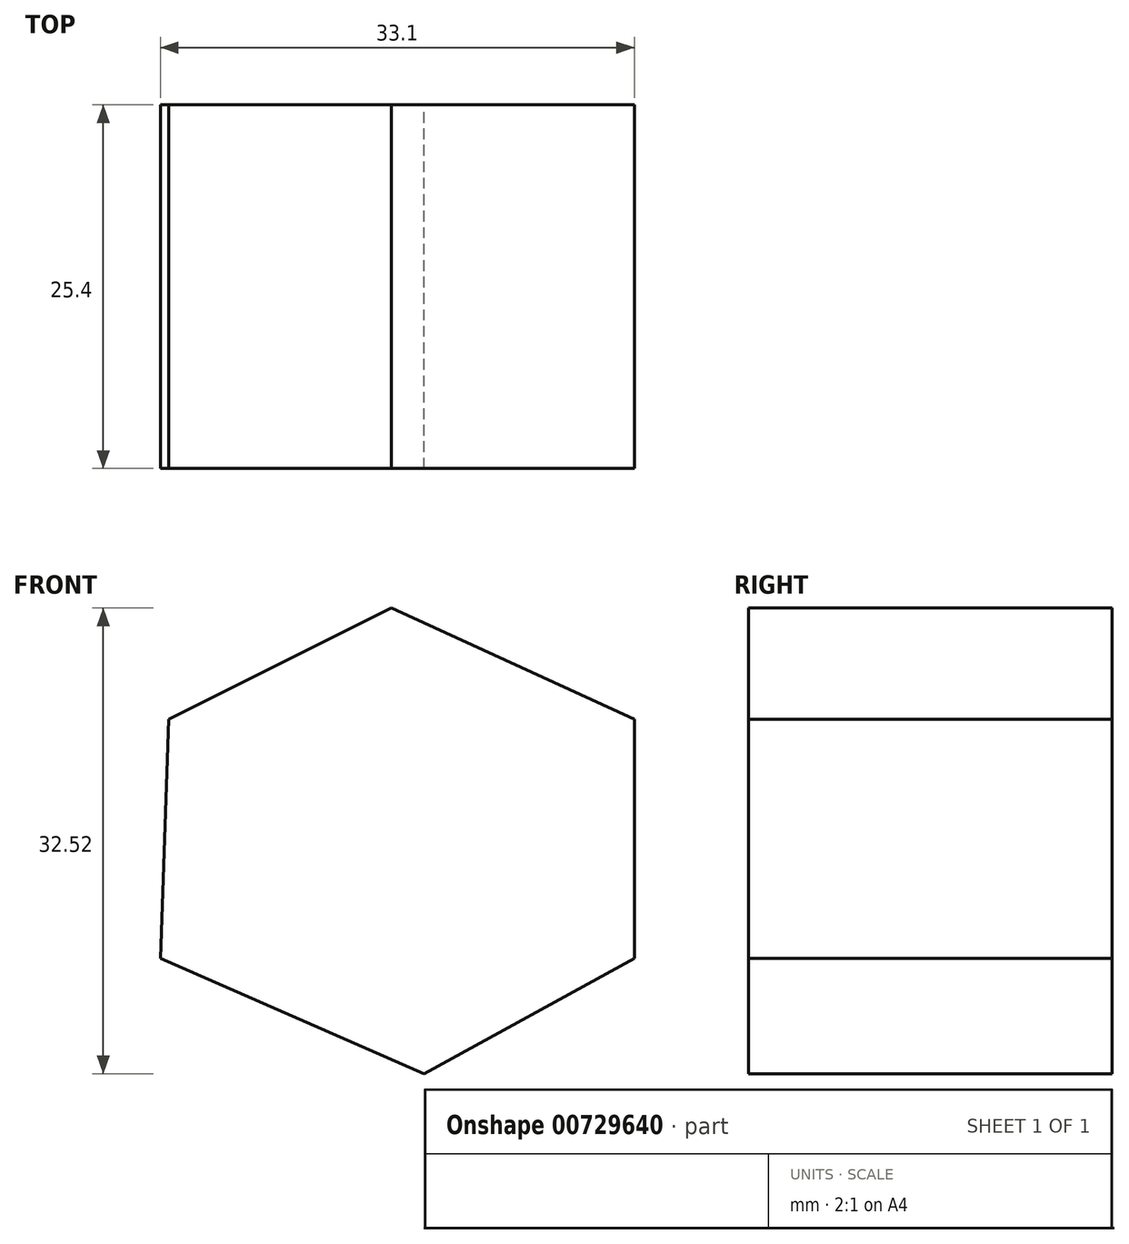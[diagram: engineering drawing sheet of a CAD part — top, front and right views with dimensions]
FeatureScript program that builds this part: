
annotation { "Feature Type Name" : "Feature", "Feature Type Description" : "" }
export const myFeature = defineFeature(function(context is Context, id is Id, definition is map)
    precondition{}
    {
        {
            var Q0;
            Q0=qCreatedBy(makeId("Front.planeOp"),FACE);
            var sketch = newSketch(context, id + "F0", { "sketchPlane" : qUnion([Q0])});
            skLineSegment(sketch, "E0", {"start": v(-58.28, 56.55) * mm, "end": v(-42.74, 64.32) * mm});
            skLineSegment(sketch, "E1", {"start": v(-42.74, 64.32) * mm, "end": v(-25.76, 56.55) * mm});
            skLineSegment(sketch, "E2", {"start": v(-25.76, 56.55) * mm, "end": v(-25.76, 39.86) * mm});
            skLineSegment(sketch, "E3", {"start": v(-25.76, 39.86) * mm, "end": v(-40.44, 31.8) * mm});
            skLineSegment(sketch, "E4", {"start": v(-40.44, 31.8) * mm, "end": v(-58.86, 39.86) * mm});
            skLineSegment(sketch, "E5", {"start": v(-58.86, 39.86) * mm, "end": v(-58.28, 56.55) * mm});
            skSolve(sketch);
        }
        {
            var Q0;
            Q0=makeQuery(id+"F0.imprint","IMPRINT",FACE,{"disambiguationData":[TD([[makeQuery(id+"F0.imprint","IMPRINT",EDGE,{"derivedFrom":sQuery(id+"F0.wireOp",EDGE,"E0")}),-1.0]])]});
            extrude(context, id + "F1", {"entities" : qUnion([Q0]), "depth" : 25.4 * mm, "offsetDistance" : 25.4 * mm});
        }
    });
